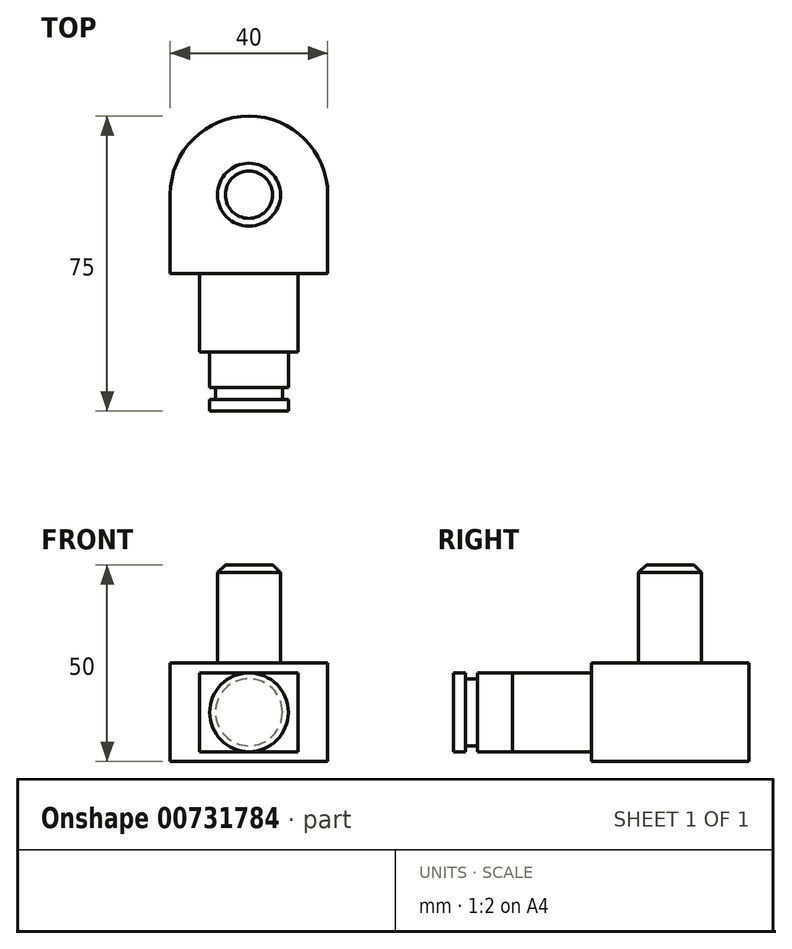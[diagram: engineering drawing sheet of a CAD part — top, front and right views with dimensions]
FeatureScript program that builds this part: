
annotation { "Feature Type Name" : "Feature", "Feature Type Description" : "" }
export const myFeature = defineFeature(function(context is Context, id is Id, definition is map)
    precondition{}
    {
        {
            var Q0;
            Q0=qCreatedBy(makeId("Top.planeOp"),FACE);
            var sketch = newSketch(context, id + "F0", { "sketchPlane" : qUnion([Q0])});
            skLineSegment(sketch, "E0.bottom", {"start": v(-20, 20) * mm, "end": v(20, 20) * mm});
            skLineSegment(sketch, "E0.top", {"start": v(-20, -20) * mm, "end": v(20, -20) * mm});
            skLineSegment(sketch, "E0.left", {"start": v(-20, 20) * mm, "end": v(-20, -20) * mm});
            skLineSegment(sketch, "E0.right", {"start": v(20, 20) * mm, "end": v(20, -20) * mm});
            skSolve(sketch);
        }
        {
            var Q0;
            Q0 = qSketchRegion(id + "F0", true);
            extrude(context, id + "F1", {"entities" : qUnion([Q0]), "depth" : 25 * mm, "offsetDistance" : 25 * mm});
        }
        {
            var Q0;
            Q0=makeQuery(id+"F1.opExtrude","SWEPT_EDGE",EDGE,{"disambiguationData":[OSD([sQuery(id+"F0.wireOp",EDGE,"E0.bottom"),sQuery(id+"F0.wireOp",EDGE,"E0.right")])]});
            var Q1;
            Q1=makeQuery(id+"F1.opExtrude","SWEPT_EDGE",EDGE,{"disambiguationData":[OSD([sQuery(id+"F0.wireOp",EDGE,"E0.bottom"),sQuery(id+"F0.wireOp",EDGE,"E0.left")])]});
            fillet(context, id + "F2", {"entities" : qUnion([Q0, Q1]), "radius" : 20 * mm, "tangentPropagation" : true, "allowEdgeOverflow" : false});
        }
        {
            var Q0;
            Q0=makeQuery(id+"F1.opExtrude","SWEPT_FACE",FACE,{"disambiguationData":[OSD([sQuery(id+"F0.wireOp",EDGE,"E0.top")])]});
            var sketch = newSketch(context, id + "F3", { "sketchPlane" : qUnion([Q0])});
            skLineSegment(sketch, "E1.bottom", {"start": v(-12.5, 22.5) * mm, "end": v(12.5, 22.5) * mm});
            skLineSegment(sketch, "E1.top", {"start": v(-12.5, 2.5) * mm, "end": v(12.5, 2.5) * mm});
            skLineSegment(sketch, "E1.left", {"start": v(-12.5, 22.5) * mm, "end": v(-12.5, 2.5) * mm});
            skLineSegment(sketch, "E1.right", {"start": v(12.5, 22.5) * mm, "end": v(12.5, 2.5) * mm});
            skSolve(sketch);
        }
        {
            var Q0;
            Q0 = qSketchRegion(id + "F3", true);
            extrude(context, id + "F4", {"entities" : qUnion([Q0]), "operationType" : NewBodyOperationType.ADD, "depth" : 20 * mm, "offsetDistance" : 25 * mm});
        }
        {
            var Q0;
            Q0=makeQuery(id+"F4.opExtrude","CAP_FACE",FACE,{"disambiguationData":[OSD([sQuery(id+"F3.wireOp",EDGE,"E1.bottom"),sQuery(id+"F3.wireOp",EDGE,"E1.top"),sQuery(id+"F3.wireOp",EDGE,"E1.left"),sQuery(id+"F3.wireOp",EDGE,"E1.right")])],"isStart":false});
            var sketch = newSketch(context, id + "F5", { "sketchPlane" : qUnion([Q0])});
            skCircle(sketch, "E2", {"center": v(0, 12.5) * mm, "radius": 10 * mm});
            skPoint(sketch, "E2.centerSnap0", {"position": v(-12.5, 12.5) * mm});
            skSolve(sketch);
        }
        {
            var Q0;
            {var subQ0=sQuery(id+"F5.wireOp",EDGE,"E2");var subQ1=makeQuery(id+"F5.imprint","INTERSECT",VERTEX,{"derivedFrom":[makeQuery(id+"F4.opExtrude","CAP_EDGE",EDGE,{"disambiguationData":[OSD([sQuery(id+"F3.wireOp",EDGE,"E1.bottom")])],"isStart":false}),subQ0]});Q0=makeQuery(id+"F5.imprint","IMPRINT",FACE,{"disambiguationData":[TD([[makeQuery(id+"F5.imprint","IMPRINT",EDGE,{"disambiguationData":[TD([[subQ1,-1.0]])],"derivedFrom":subQ0}),1.0]])]});}
            extrude(context, id + "F6", {"entities" : qUnion([Q0]), "operationType" : NewBodyOperationType.ADD, "depth" : 15 * mm, "offsetDistance" : 25 * mm});
        }
        {
            var Q0;
            Q0=makeQuery(id+"F1.opExtrude","CAP_FACE",FACE,{"disambiguationData":[OSD([sQuery(id+"F0.wireOp",EDGE,"E0.bottom"),sQuery(id+"F0.wireOp",EDGE,"E0.top"),sQuery(id+"F0.wireOp",EDGE,"E0.left"),sQuery(id+"F0.wireOp",EDGE,"E0.right")])],"isStart":false});
            var sketch = newSketch(context, id + "F7", { "sketchPlane" : qUnion([Q0])});
            skCircle(sketch, "E3", {"center": v(0, 0) * mm, "radius": 8 * mm});
            skSolve(sketch);
        }
        {
            var Q0;
            Q0=makeQuery(id+"F7.imprint","IMPRINT",FACE,{"disambiguationData":[TD([[makeQuery(id+"F7.imprint","IMPRINT",EDGE,{"derivedFrom":sQuery(id+"F7.wireOp",EDGE,"E3")}),1.0]])]});
            extrude(context, id + "F8", {"entities" : qUnion([Q0]), "operationType" : NewBodyOperationType.ADD, "depth" : 25 * mm, "offsetDistance" : 25 * mm});
        }
        {
            var Q0;
            Q0=makeQuery(id+"F8.opExtrude","CAP_EDGE",EDGE,{"disambiguationData":[OSD([sQuery(id+"F7.wireOp",EDGE,"E3")])],"isStart":false});
            chamfer(context, id + "F9", {"entities" : qUnion([Q0]), "width" : 2 * mm, "tangentPropagation" : true});
        }
        {
            var Q0;
            Q0=qCreatedBy(makeId("Right.planeOp"),FACE);
            var sketch = newSketch(context, id + "F10", { "sketchPlane" : qUnion([Q0])});
            skLineSegment(sketch, "E4.bottom", {"start": v(-52, 24) * mm, "end": v(-49, 24) * mm});
            skLineSegment(sketch, "E4.top", {"start": v(-52, 21) * mm, "end": v(-49, 21) * mm});
            skLineSegment(sketch, "E4.left", {"start": v(-52, 24) * mm, "end": v(-52, 21) * mm});
            skLineSegment(sketch, "E4.right", {"start": v(-49, 24) * mm, "end": v(-49, 21) * mm});
            skSolve(sketch);
        }
        {
            var Q0;
            Q0=makeQuery(id+"F10.imprint","IMPRINT",FACE,{"disambiguationData":[TD([[makeQuery(id+"F10.imprint","IMPRINT",EDGE,{"derivedFrom":sQuery(id+"F10.wireOp",EDGE,"E4.bottom")}),-1.0]])]});
            var Q1;
            Q1=makeQuery(id+"F6.opExtrude","SWEPT_FACE",FACE,{"disambiguationData":[OSD([sQuery(id+"F5.wireOp",EDGE,"E2")])]});
            revolve(context, id + "F11", {"operationType" : NewBodyOperationType.REMOVE, "surfaceOperationType" : NewSurfaceOperationType.NEW, "entities" : qUnion([Q0]), "axis" : qUnion([Q1]), "revolveType" : RevolveType.FULL, "oppositeDirection" : true});
        }
    });
